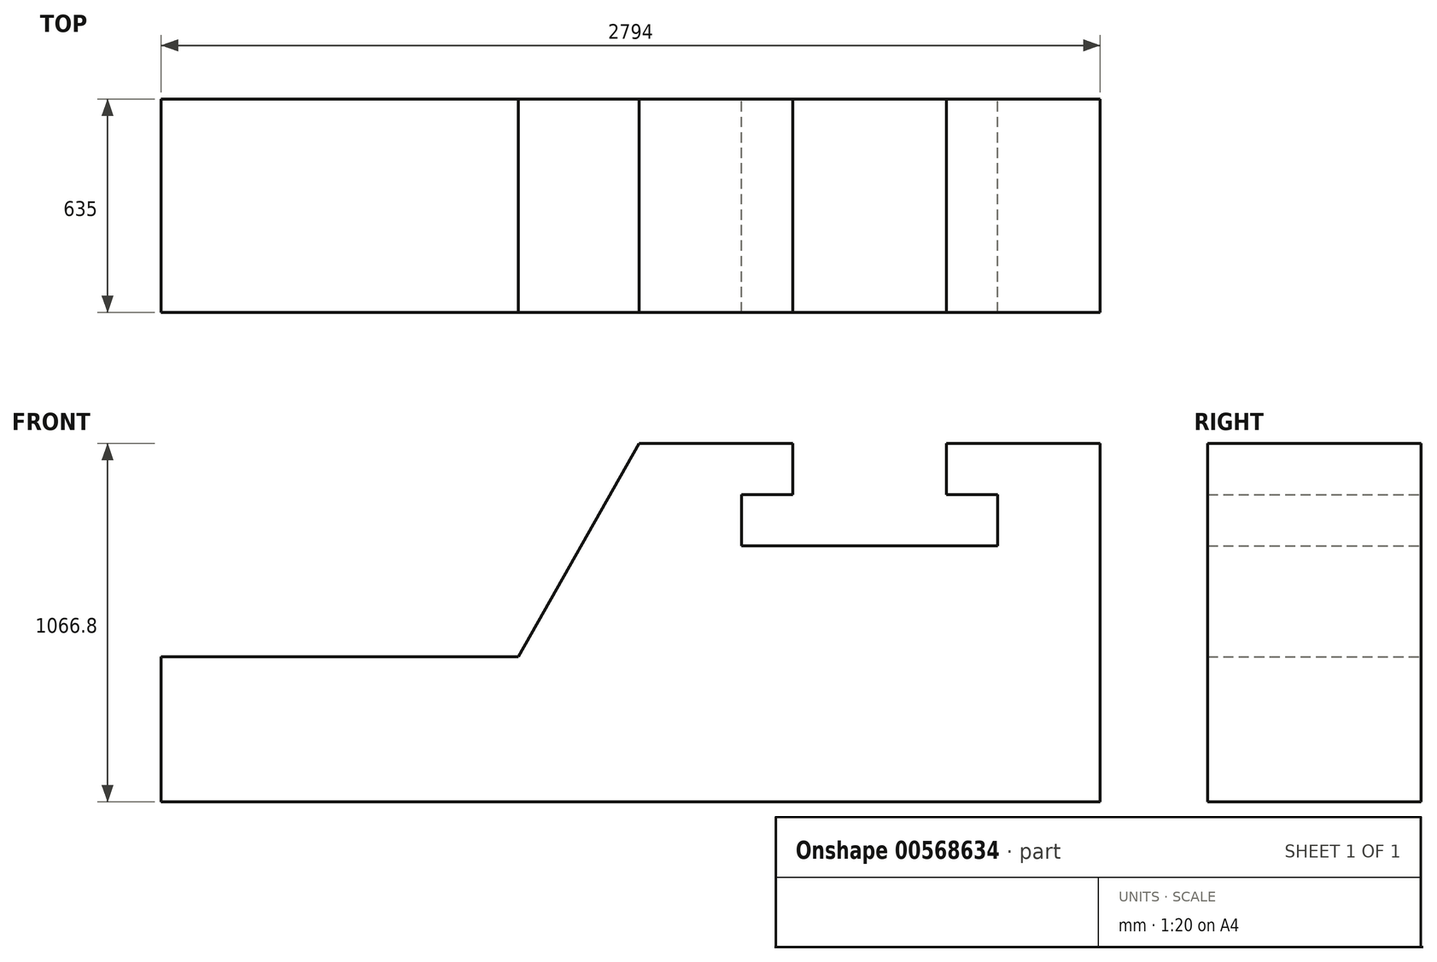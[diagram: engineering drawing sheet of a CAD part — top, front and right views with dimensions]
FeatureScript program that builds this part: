
annotation { "Feature Type Name" : "Feature", "Feature Type Description" : "" }
export const myFeature = defineFeature(function(context is Context, id is Id, definition is map)
    precondition{}
    {
        {
            var Q0;
            Q0=qCreatedBy(makeId("Front.planeOp"),FACE);
            var sketch = newSketch(context, id + "F0", { "sketchPlane" : qUnion([Q0])});
            skLineSegment(sketch, "E0", {"start": v(0, 0) * mm, "end": v(0, 635) * mm});
            skLineSegment(sketch, "E1", {"start": v(0, 635) * mm, "end": v(-457.2, 635) * mm});
            skLineSegment(sketch, "E2", {"start": v(-457.2, 635) * mm, "end": v(-457.2, 482.6) * mm});
            skLineSegment(sketch, "E3", {"start": v(-457.2, 482.6) * mm, "end": v(-304.8, 482.6) * mm});
            skLineSegment(sketch, "E4", {"start": v(-304.8, 482.6) * mm, "end": v(-304.8, 330.2) * mm});
            skLineSegment(sketch, "E5", {"start": v(-304.8, 330.2) * mm, "end": v(-1066.8, 330.2) * mm});
            skLineSegment(sketch, "E6", {"start": v(-1066.8, 330.2) * mm, "end": v(-1066.8, 482.6) * mm});
            skLineSegment(sketch, "E7", {"start": v(-1066.8, 482.6) * mm, "end": v(-914.4, 482.6) * mm});
            skLineSegment(sketch, "E8", {"start": v(-914.4, 482.6) * mm, "end": v(-914.4, 635) * mm});
            skLineSegment(sketch, "E9", {"start": v(-914.4, 635) * mm, "end": v(-1371.6, 635) * mm});
            skLineSegment(sketch, "E10", {"start": v(-1371.6, 635) * mm, "end": v(-1731.29, 0) * mm});
            skLineSegment(sketch, "E11", {"start": v(-1731.29, 0) * mm, "end": v(0, 0) * mm});
            skSolve(sketch);
        }
        {
            var Q0;
            Q0=makeQuery(id+"F0.imprint","IMPRINT",FACE,{"disambiguationData":[TD([[makeQuery(id+"F0.imprint","IMPRINT",EDGE,{"derivedFrom":sQuery(id+"F0.wireOp",EDGE,"E0")}),1.0]])]});
            var sketch = newSketch(context, id + "F1", { "sketchPlane" : qUnion([Q0])});
            skLineSegment(sketch, "E12", {"start": v(0, 0) * mm, "end": v(-1524, 0) * mm});
            skLineSegment(sketch, "E13", {"start": v(-1524, 0) * mm, "end": v(-2540, 0) * mm});
            skLineSegment(sketch, "E14", {"start": v(-2540, 0) * mm, "end": v(-2794, 0) * mm});
            skLineSegment(sketch, "E15", {"start": v(-2794, 0) * mm, "end": v(-2794, -431.8) * mm});
            skLineSegment(sketch, "E16", {"start": v(-2794, -431.8) * mm, "end": v(0, -431.8) * mm});
            skLineSegment(sketch, "E17", {"start": v(0, -431.8) * mm, "end": v(0, 0) * mm});
            skSolve(sketch);
        }
        {
            var Q0;
            {var subQ3=sQuery(id+"F1.wireOp",EDGE,"E12");Q0=makeQuery(id+"F1.imprint","IMPRINT",FACE,{"disambiguationData":[TD([[makeQuery(id+"F1.imprint","IMPRINT",EDGE,{"derivedFrom":subQ3}),-1.0]])]});}
            extrude(context, id + "F2", {"entities" : qUnion([Q0]), "depth" : 635 * mm, "offsetDistance" : 25.4 * mm});
        }
        {
            var Q0;
            Q0=makeQuery(id+"F0.imprint","IMPRINT",FACE,{"disambiguationData":[TD([[makeQuery(id+"F0.imprint","IMPRINT",EDGE,{"derivedFrom":sQuery(id+"F0.wireOp",EDGE,"E0")}),1.0]])]});
            extrude(context, id + "F3", {"entities" : qUnion([Q0]), "operationType" : NewBodyOperationType.ADD, "depth" : 635 * mm, "offsetDistance" : 25.4 * mm});
        }
    });
